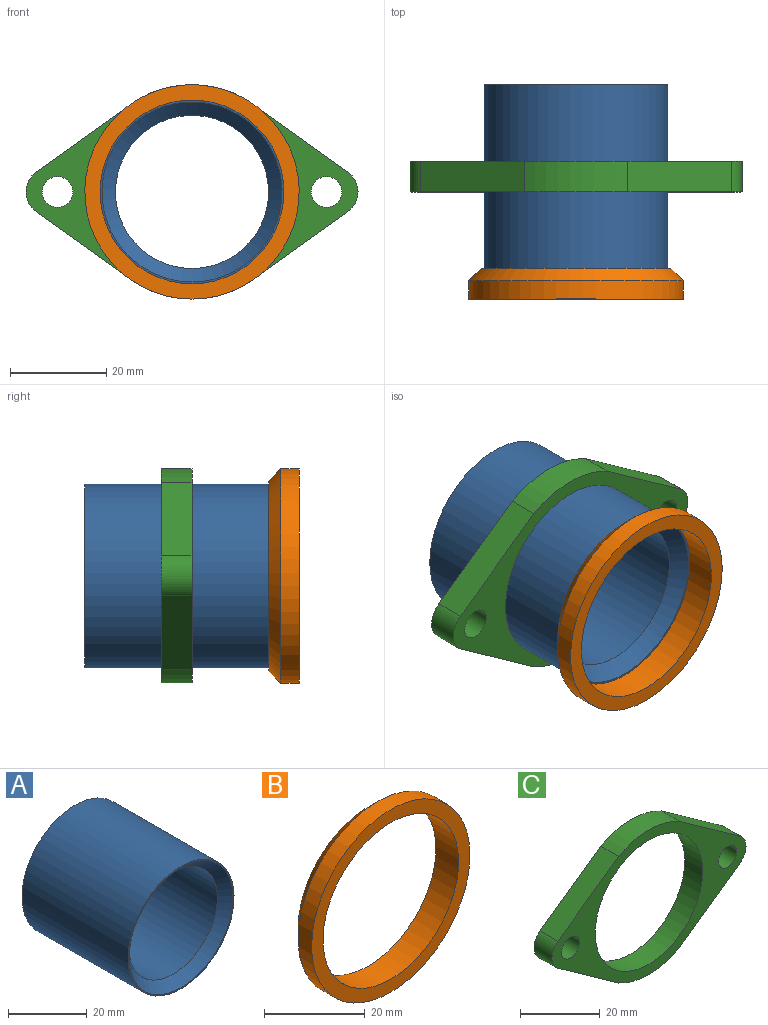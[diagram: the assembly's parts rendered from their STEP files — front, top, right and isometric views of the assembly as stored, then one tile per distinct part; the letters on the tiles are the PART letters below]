
ASSEMBLY  parts=3 mates=2
PART A: 5 faces, bbox 38.1x38.1x38.1 mm
  f0: cylinder r=15.88mm len=35.31mm, axis (0,1,0), area 3521.6mm2, adj f3,f4
  f1: cylinder r=19.05mm len=38.1mm, axis (0,1,0), area 4560.4mm2, adj f2,f3
  f2: plane 38.1x38.1mm, normal (0,-1,0), area 45.1mm2, adj f1,f4
  f3: plane 38.1x38.1mm, normal (0,1,0), area 348.4mm2, adj f0,f1
  f4: cone r=15.88mm half-angle=45deg, axis (0,-1,0), area 428.8mm2, adj f0,f2
PART B: 5 faces, bbox 44.5x6.4x44.5 mm
  f0: cylinder r=19.05mm len=38.1mm, axis (0,1,0), area 760.1mm2, adj f2,f3
  f1: cylinder r=22.23mm len=44.45mm, axis (0,1,0), area 532mm2, adj f2,f4
  f2: plane 44.45x44.45mm, normal (0,-1,0), area 411.7mm2, adj f0,f1
  f3: plane 39.37x39.37mm, normal (0,1,0), area 77.3mm2, adj f0,f4
  f4: cone r=22.23mm half-angle=45deg, axis (0,-1,0), area 473mm2, adj f1,f3
PART C: 13 faces, bbox 68.8x6.4x44.5 mm
  f0: plane 21.5x15.3mm, normal (-0.58,0,0.81), area 167.6mm2, adj f7,f9,f10,f11
  f1: plane 21.5x15.3mm, normal (-0.58,0,-0.81), area 167.6mm2, adj f2,f9,f10,f11
  f2: cylinder r=22.23mm len=21.55mm, axis (0,1,0), area 142.9mm2, adj f1,f3,f9,f10
  f3: plane 21.5x15.3mm, normal (0.58,0,-0.81), area 167.6mm2, adj f2,f9,f10,f12
  f4: plane 21.5x15.3mm, normal (0.58,0,0.81), area 167.6mm2, adj f7,f9,f10,f12
  f5: cylinder r=19.05mm len=38.1mm, axis (0,1,0), area 760.1mm2, adj f9,f10
  f6: cylinder r=3.17mm len=6.35mm, axis (0,1,0), area 126.7mm2, adj f9,f10
  f7: cylinder r=22.23mm len=21.55mm, axis (0,1,0), area 142.9mm2, adj f0,f4,f9,f10
  f8: cylinder r=3.17mm len=6.35mm, axis (0,1,0), area 126.7mm2, adj f9,f10
  f9: plane 68.83x44.45mm, normal (0,-1,0), area 754.4mm2, adj f0,f1,f2,f3,f4,f5,f6,f7
  f10: plane 68.83x44.45mm, normal (0,1,0), area 754.4mm2, adj f0,f1,f2,f3,f4,f5,f6,f7
  f11: cylinder r=5.08mm len=8.28mm, axis (0,-1,0), area 61.4mm2, adj f0,f1,f9,f10
  f12: cylinder r=5.08mm len=8.28mm, axis (0,1,0), area 61.4mm2, adj f3,f4,f9,f10
PLACE A t=(1.37,-0.11,-0.43)mm
PLACE B t=(1.37,-0.11,-0.43)mm
PLACE C t=(16.8,-15.99,-6.68)mm
MATE fastened C.f2 <-> A.f0  axis (0,1,0) through (-26.12,-19.16,30.02)mm
MATE fastened B.f0 <-> A.f0  axis (0,1,0) through (-26.12,-38.21,30.02)mm
